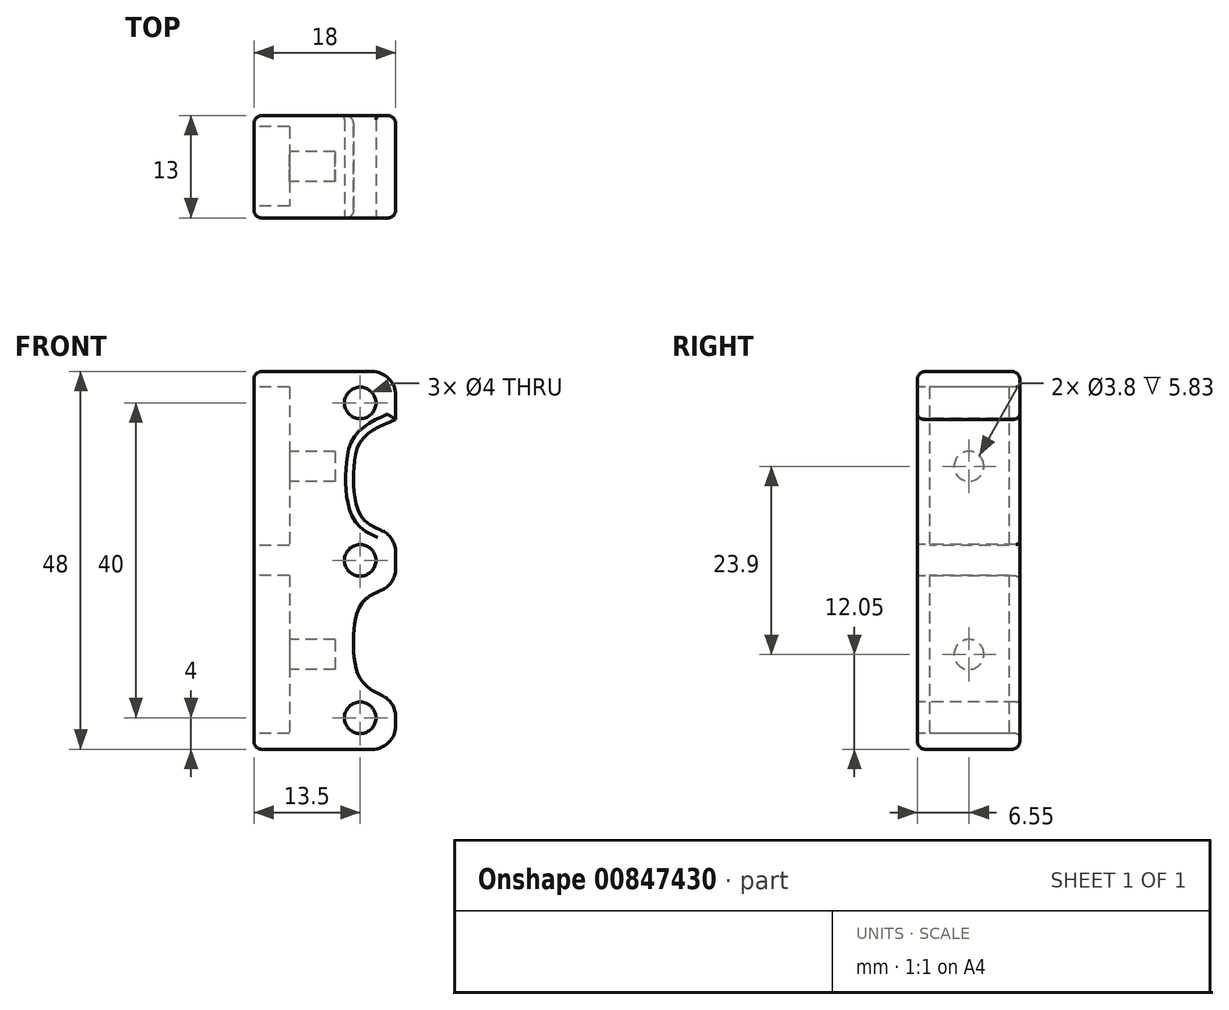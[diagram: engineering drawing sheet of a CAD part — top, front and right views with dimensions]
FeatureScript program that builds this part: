
annotation { "Feature Type Name" : "Feature", "Feature Type Description" : "" }
export const myFeature = defineFeature(function(context is Context, id is Id, definition is map)
    precondition{}
    {
        {
            var Q0;
            Q0=qCreatedBy(makeId("Front.planeOp"),FACE);
            var sketch = newSketch(context, id + "F0", { "sketchPlane" : qUnion([Q0])});
            skLineSegment(sketch, "E0.bottom", {"start": v(0, 24) * mm, "end": v(18, 24) * mm});
            skLineSegment(sketch, "E0.top", {"start": v(0, -24) * mm, "end": v(18, -24) * mm});
            skLineSegment(sketch, "E0.left", {"start": v(0, 24) * mm, "end": v(0, -24) * mm});
            skLineSegment(sketch, "E0.right", {"start": v(18, 24) * mm, "end": v(18, -24) * mm});
            skSolve(sketch);
        }
        {
            var Q0;
            Q0=qSketchRegion(id+"F0",true);
            extrude(context, id + "F1", {"entities" : qUnion([Q0]), "depth" : 13 * mm, "offsetDistance" : 25 * mm});
        }
        {
            var Q0;
            Q0=makeQuery(id+"F1.opExtrude","CAP_FACE",FACE,{"disambiguationData":[OSD([sQuery(id+"F0.wireOp",EDGE,"E0.bottom"),sQuery(id+"F0.wireOp",EDGE,"E0.top"),sQuery(id+"F0.wireOp",EDGE,"E0.left"),sQuery(id+"F0.wireOp",EDGE,"E0.right")])],"isStart":false});
            var sketch = newSketch(context, id + "F2", { "sketchPlane" : qUnion([Q0])});
            skCircle(sketch, "E1", {"center": v(13.5, 0) * mm, "radius": 2 * mm});
            skCircle(sketch, "E2", {"center": v(13.5, -20) * mm, "radius": 2 * mm});
            skCircle(sketch, "E3", {"center": v(13.5, 20) * mm, "radius": 2 * mm});
            skLineSegment(sketch, "E4", {"start": v(13.5, 20) * mm, "end": v(13.5, -20) * mm, "construction": true});
            skSolve(sketch);
        }
        {
            var Q0;
            Q0=qSketchRegion(id+"F2",true);
            extrude(context, id + "F3", {"entities" : qUnion([Q0]), "operationType" : NewBodyOperationType.REMOVE, "oppositeDirection" : true, "depth" : 25 * mm, "offsetDistance" : 25 * mm});
        }
        {
            var Q0;
            Q0=makeQuery(id+"F1.opExtrude","SWEPT_EDGE",EDGE,{"disambiguationData":[OSD([sQuery(id+"F0.wireOp",EDGE,"E0.bottom"),sQuery(id+"F0.wireOp",EDGE,"E0.right")])]});
            var Q1;
            Q1=makeQuery(id+"F1.opExtrude","SWEPT_EDGE",EDGE,{"disambiguationData":[OSD([sQuery(id+"F0.wireOp",EDGE,"E0.top"),sQuery(id+"F0.wireOp",EDGE,"E0.right")])]});
            fillet(context, id + "F4", {"entities" : qUnion([Q0, Q1]), "radius" : 3 * mm, "tangentPropagation" : true, "allowEdgeOverflow" : false});
        }
        {
            var Q0;
            Q0=makeQuery(id+"F1.opExtrude","CAP_FACE",FACE,{"disambiguationData":[OSD([sQuery(id+"F0.wireOp",EDGE,"E0.bottom"),sQuery(id+"F0.wireOp",EDGE,"E0.top"),sQuery(id+"F0.wireOp",EDGE,"E0.left"),sQuery(id+"F0.wireOp",EDGE,"E0.right")])],"isStart":false});
            var sketch = newSketch(context, id + "F5", { "sketchPlane" : qUnion([Q0])});
            skFitSpline(sketch, "E5", {"points": [v(18, 17.89) * mm, v(12.86, 13.22) * mm, v(13, 7.08) * mm, v(18, 3.24) * mm], "startDerivative": vector(-35.06, -13.2) * mm, "endDerivative": vector(33.67, -8.91) * mm});
            skFitSpline(sketch, "E6.MirrorCS", {"points": [v(18, -17.89) * mm, v(12.86, -13.22) * mm, v(13, -7.08) * mm, v(18, -3.24) * mm], "startDerivative": vector(-35.06, 13.2) * mm, "endDerivative": vector(33.67, 8.91) * mm});
            skLineSegment(sketch, "E7", {"start": v(18, 17.89) * mm, "end": v(18, 3.24) * mm});
            skLineSegment(sketch, "E8", {"start": v(18, -3.24) * mm, "end": v(18, -17.89) * mm});
            skSolve(sketch);
        }
        {
            var Q0;
            Q0=qSketchRegion(id+"F5",true);
            extrude(context, id + "F6", {"entities" : qUnion([Q0]), "operationType" : NewBodyOperationType.REMOVE, "oppositeDirection" : true, "depth" : 25 * mm, "offsetDistance" : 25 * mm});
        }
        {
            var Q0;
            {var subQ0=sQuery(id+"F5.wireOp",EDGE,"E7");var subQ1=sQuery(id+"F5.wireOp",EDGE,"E5");var subQ2=sQuery(id+"F0.wireOp",EDGE,"E0.right");Q0=makeQuery(id+"F6.boolean.opBoolean","COPY",EDGE,{"derivedFrom":makeQuery(id+"F6.opExtrude","SWEPT_EDGE",EDGE,{"disambiguationData":[OSD([subQ2,subQ1,subQ0]),TDD([makeQuery(id+"F5.imprint","INTERSECT",VERTEX,{"disambiguationData":[OD(0.0)],"derivedFrom":[makeQuery(id+"F1.opExtrude","CAP_EDGE",EDGE,{"disambiguationData":[OSD([subQ2])],"isStart":false}),subQ1,subQ0]})])]})});}
            var Q1;
            {var subQ0=sQuery(id+"F5.wireOp",EDGE,"E8");var subQ1=sQuery(id+"F5.wireOp",EDGE,"E6.MirrorCS");var subQ2=sQuery(id+"F0.wireOp",EDGE,"E0.right");Q1=makeQuery(id+"F6.boolean.opBoolean","COPY",EDGE,{"derivedFrom":makeQuery(id+"F6.opExtrude","SWEPT_EDGE",EDGE,{"disambiguationData":[OSD([subQ2,subQ1,subQ0]),TDD([makeQuery(id+"F5.imprint","INTERSECT",VERTEX,{"disambiguationData":[OD(1.0)],"derivedFrom":[makeQuery(id+"F1.opExtrude","CAP_EDGE",EDGE,{"disambiguationData":[OSD([subQ2])],"isStart":false}),subQ1,subQ0]})])]})});}
            var Q2;
            {var subQ0=sQuery(id+"F5.wireOp",EDGE,"E7");var subQ1=sQuery(id+"F5.wireOp",EDGE,"E5");var subQ2=sQuery(id+"F0.wireOp",EDGE,"E0.right");Q2=makeQuery(id+"F6.boolean.opBoolean","COPY",EDGE,{"derivedFrom":makeQuery(id+"F6.opExtrude","SWEPT_EDGE",EDGE,{"disambiguationData":[OSD([subQ2,subQ1,subQ0]),TDD([makeQuery(id+"F5.imprint","INTERSECT",VERTEX,{"disambiguationData":[OD(1.0)],"derivedFrom":[makeQuery(id+"F1.opExtrude","CAP_EDGE",EDGE,{"disambiguationData":[OSD([subQ2])],"isStart":false}),subQ1,subQ0]})])]})});}
            var Q3;
            {var subQ0=sQuery(id+"F5.wireOp",EDGE,"E8");var subQ1=sQuery(id+"F5.wireOp",EDGE,"E6.MirrorCS");var subQ2=sQuery(id+"F0.wireOp",EDGE,"E0.right");Q3=makeQuery(id+"F6.boolean.opBoolean","COPY",EDGE,{"derivedFrom":makeQuery(id+"F6.opExtrude","SWEPT_EDGE",EDGE,{"disambiguationData":[OSD([subQ2,subQ1,subQ0]),TDD([makeQuery(id+"F5.imprint","INTERSECT",VERTEX,{"disambiguationData":[OD(0.0)],"derivedFrom":[makeQuery(id+"F1.opExtrude","CAP_EDGE",EDGE,{"disambiguationData":[OSD([subQ2])],"isStart":false}),subQ1,subQ0]})])]})});}
            fillet(context, id + "F7", {"entities" : qUnion([Q0, Q1, Q2, Q3]), "radius" : 3 * mm, "tangentPropagation" : true, "allowEdgeOverflow" : false});
        }
        {
            var Q0;
            Q0=makeQuery(id+"F1.opExtrude","SWEPT_EDGE",EDGE,{"disambiguationData":[OSD([sQuery(id+"F0.wireOp",EDGE,"E0.top"),sQuery(id+"F0.wireOp",EDGE,"E0.left")])]});
            var Q1;
            Q1=makeQuery(id+"F1.opExtrude","SWEPT_EDGE",EDGE,{"disambiguationData":[OSD([sQuery(id+"F0.wireOp",EDGE,"E0.bottom"),sQuery(id+"F0.wireOp",EDGE,"E0.left")])]});
            fillet(context, id + "F8", {"entities" : qUnion([Q0, Q1]), "radius" : 1 * mm, "tangentPropagation" : true, "allowEdgeOverflow" : false});
        }
        {
            var Q0;
            Q0=makeQuery(id+"F1.opExtrude","CAP_EDGE",EDGE,{"disambiguationData":[OSD([sQuery(id+"F0.wireOp",EDGE,"E0.bottom")])],"isStart":false});
            var Q1;
            Q1=makeQuery(id+"F1.opExtrude","CAP_EDGE",EDGE,{"disambiguationData":[OSD([sQuery(id+"F0.wireOp",EDGE,"E0.left")])],"isStart":true});
            fillet(context, id + "F9", {"entities" : qUnion([Q0, Q1]), "radius" : 1 * mm, "tangentPropagation" : true, "allowEdgeOverflow" : false});
        }
        {
            var Q0;
            Q0=makeQuery(id+"F3.boolean.opBoolean","COPY",EDGE,{"derivedFrom":makeQuery(id+"F3.opExtrude","CAP_EDGE",EDGE,{"disambiguationData":[OSD([sQuery(id+"F2.wireOp",EDGE,"E2")])],"isStart":true})});
            var Q1;
            Q1=makeQuery(id+"F3.boolean.opBoolean","COPY",EDGE,{"derivedFrom":makeQuery(id+"F3.opExtrude","CAP_EDGE",EDGE,{"disambiguationData":[OSD([sQuery(id+"F2.wireOp",EDGE,"E1")])],"isStart":true})});
            var Q2;
            Q2=makeQuery(id+"F3.boolean.opBoolean","COPY",EDGE,{"derivedFrom":makeQuery(id+"F3.opExtrude","CAP_EDGE",EDGE,{"disambiguationData":[OSD([sQuery(id+"F2.wireOp",EDGE,"E3")])],"isStart":true})});
            var Q3;
            Q3=makeQuery(id+"F3.boolean.opBoolean","INTERSECT",EDGE,{"derivedFrom":[makeQuery(id+"F1.opExtrude","CAP_FACE",FACE,{"disambiguationData":[OSD([sQuery(id+"F0.wireOp",EDGE,"E0.bottom"),sQuery(id+"F0.wireOp",EDGE,"E0.top"),sQuery(id+"F0.wireOp",EDGE,"E0.left"),sQuery(id+"F0.wireOp",EDGE,"E0.right")])],"isStart":true}),makeQuery(id+"F3.opExtrude","SWEPT_FACE",FACE,{"disambiguationData":[OSD([sQuery(id+"F2.wireOp",EDGE,"E3")])]})]});
            var Q4;
            Q4=makeQuery(id+"F3.boolean.opBoolean","INTERSECT",EDGE,{"derivedFrom":[makeQuery(id+"F1.opExtrude","CAP_FACE",FACE,{"disambiguationData":[OSD([sQuery(id+"F0.wireOp",EDGE,"E0.bottom"),sQuery(id+"F0.wireOp",EDGE,"E0.top"),sQuery(id+"F0.wireOp",EDGE,"E0.left"),sQuery(id+"F0.wireOp",EDGE,"E0.right")])],"isStart":true}),makeQuery(id+"F3.opExtrude","SWEPT_FACE",FACE,{"disambiguationData":[OSD([sQuery(id+"F2.wireOp",EDGE,"E1")])]})]});
            var Q5;
            Q5=makeQuery(id+"F3.boolean.opBoolean","INTERSECT",EDGE,{"derivedFrom":[makeQuery(id+"F1.opExtrude","CAP_FACE",FACE,{"disambiguationData":[OSD([sQuery(id+"F0.wireOp",EDGE,"E0.bottom"),sQuery(id+"F0.wireOp",EDGE,"E0.top"),sQuery(id+"F0.wireOp",EDGE,"E0.left"),sQuery(id+"F0.wireOp",EDGE,"E0.right")])],"isStart":true}),makeQuery(id+"F3.opExtrude","SWEPT_FACE",FACE,{"disambiguationData":[OSD([sQuery(id+"F2.wireOp",EDGE,"E2")])]})]});
            fillet(context, id + "F10", {"entities" : qUnion([Q0, Q1, Q2, Q3, Q4, Q5]), "radius" : 0.5 * mm, "tangentPropagation" : true, "allowEdgeOverflow" : false});
        }
        {
            var Q0;
            Q0=makeQuery(id+"F1.opExtrude","SWEPT_FACE",FACE,{"disambiguationData":[OSD([sQuery(id+"F0.wireOp",EDGE,"E0.left")])]});
            var sketch = newSketch(context, id + "F11", { "sketchPlane" : qUnion([Q0])});
            skLineSegment(sketch, "E9.bottom", {"start": v(1.4, 22) * mm, "end": v(11.5, 22) * mm});
            skLineSegment(sketch, "E9.top", {"start": v(1.4, 1.9) * mm, "end": v(11.5, 1.9) * mm});
            skLineSegment(sketch, "E9.left", {"start": v(1.4, 22) * mm, "end": v(1.4, 1.9) * mm});
            skLineSegment(sketch, "E9.right", {"start": v(11.5, 22) * mm, "end": v(11.5, 1.9) * mm});
            skLineSegment(sketch, "E10.bottom", {"start": v(1.4, -1.9) * mm, "end": v(11.5, -1.9) * mm});
            skLineSegment(sketch, "E10.top", {"start": v(1.4, -22) * mm, "end": v(11.5, -22) * mm});
            skLineSegment(sketch, "E10.left", {"start": v(1.4, -1.9) * mm, "end": v(1.4, -22) * mm});
            skLineSegment(sketch, "E10.right", {"start": v(11.5, -1.9) * mm, "end": v(11.5, -22) * mm});
            skSolve(sketch);
        }
        {
            var Q0;
            Q0=qSketchRegion(id+"F11",true);
            extrude(context, id + "F12", {"entities" : qUnion([Q0]), "operationType" : NewBodyOperationType.REMOVE, "oppositeDirection" : true, "depth" : 4.5 * mm, "offsetDistance" : 25 * mm});
        }
        {
            var Q0;
            Q0=makeQuery(id+"F12.boolean.opBoolean","COPY",FACE,{"derivedFrom":makeQuery(id+"F12.opExtrude","CAP_FACE",FACE,{"disambiguationData":[OSD([sQuery(id+"F11.wireOp",EDGE,"E9.bottom"),sQuery(id+"F11.wireOp",EDGE,"E9.top"),sQuery(id+"F11.wireOp",EDGE,"E9.left"),sQuery(id+"F11.wireOp",EDGE,"E9.right")])],"isStart":false})});
            var sketch = newSketch(context, id + "F13", { "sketchPlane" : qUnion([Q0])});
            skLineSegment(sketch, "E11", {"start": v(6.45, 22) * mm, "end": v(6.45, 1.9) * mm, "construction": true});
            skLineSegment(sketch, "E12", {"start": v(11.5, 11.95) * mm, "end": v(1.4, 11.95) * mm, "construction": true});
            skCircle(sketch, "E13", {"center": v(6.45, 11.95) * mm, "radius": 1.9 * mm});
            skSolve(sketch);
        }
        {
            var Q0;
            Q0=makeQuery(id+"F12.boolean.opBoolean","COPY",FACE,{"derivedFrom":makeQuery(id+"F12.opExtrude","CAP_FACE",FACE,{"disambiguationData":[OSD([sQuery(id+"F11.wireOp",EDGE,"E10.bottom"),sQuery(id+"F11.wireOp",EDGE,"E10.top"),sQuery(id+"F11.wireOp",EDGE,"E10.left"),sQuery(id+"F11.wireOp",EDGE,"E10.right")])],"isStart":false})});
            var sketch = newSketch(context, id + "F14", { "sketchPlane" : qUnion([Q0])});
            skLineSegment(sketch, "E14", {"start": v(11.5, -11.95) * mm, "end": v(1.4, -11.95) * mm});
            skLineSegment(sketch, "E15", {"start": v(6.45, -1.9) * mm, "end": v(6.45, -22) * mm});
            skCircle(sketch, "E16", {"center": v(6.45, -11.95) * mm, "radius": 1.9 * mm});
            skSolve(sketch);
        }
        {
            var Q0;
            Q0 = qSketchRegion(id + "F13", true);
            var Q1;
            Q1 = qSketchRegion(id + "F14", true);
            extrude(context, id + "F15", {"entities" : qUnion([Q0, Q1]), "operationType" : NewBodyOperationType.REMOVE, "oppositeDirection" : true, "depth" : 5.83 * mm, "offsetDistance" : 25 * mm});
        }
    });
